# Revit family: LeL Spot 3.0 316L
name_source: partatom
category: Lighting Fixtures
units: mm (PartAtom-declared; Revit-internal decimal feet)

## family parameters
Always vertical = No
Cut with Voids When Loaded = No
Light Source = No
OmniClass Number = 23.80.70.00
OmniClass Title = Lighting
Part Type = Normal
Room Calculation Point = No
Round Connector Dimension = Use Diameter
Shared = No
Work Plane-Based = Yes

## types (6) — shared parameters
CCT = 3000 K
CRI = CRI80
Default Elevation = 1219 mm
Description = Underwater Projectors
IK = IK09
IP = IP68
Lamp = LED
Manufacturer = L&L Luce&Light srl
Model = PW30
Rated Power supply = 24 V
URL = www.lucelight.it/en/prodotto.php/1282
Weight = 3.05 kg

## per-type parameters (varying)
| type | Apparent Load | Lumen Output | Photometry | Wattage |
| S 10° 12W | 12 VA | 593 lm | PW30 Light source : S 10° 12W | 12 W |
| M 20° 12W | 12 VA | 596 lm | PW30 Light source : M 20° 12W | 12 W |
| L 40° 12W | 12 VA | 521 lm | PW30 Light source : L 40° 12W | 12 W |
| S 10° 18W | 18 VA | 893 lm | PW30 Light source : S 10° 12W | 18 W |
| M 20° 18W | 18 VA | 893 lm | PW30 Light source : M 20° 18W | 18 W |
| L 40° 18W | 18 VA | 782 lm | PW30 Light source : L 40° 18W | 18 W |

## geometry (parser evidence)
native form markers: Sweep x1
no freeform markers — native parametric forms only
